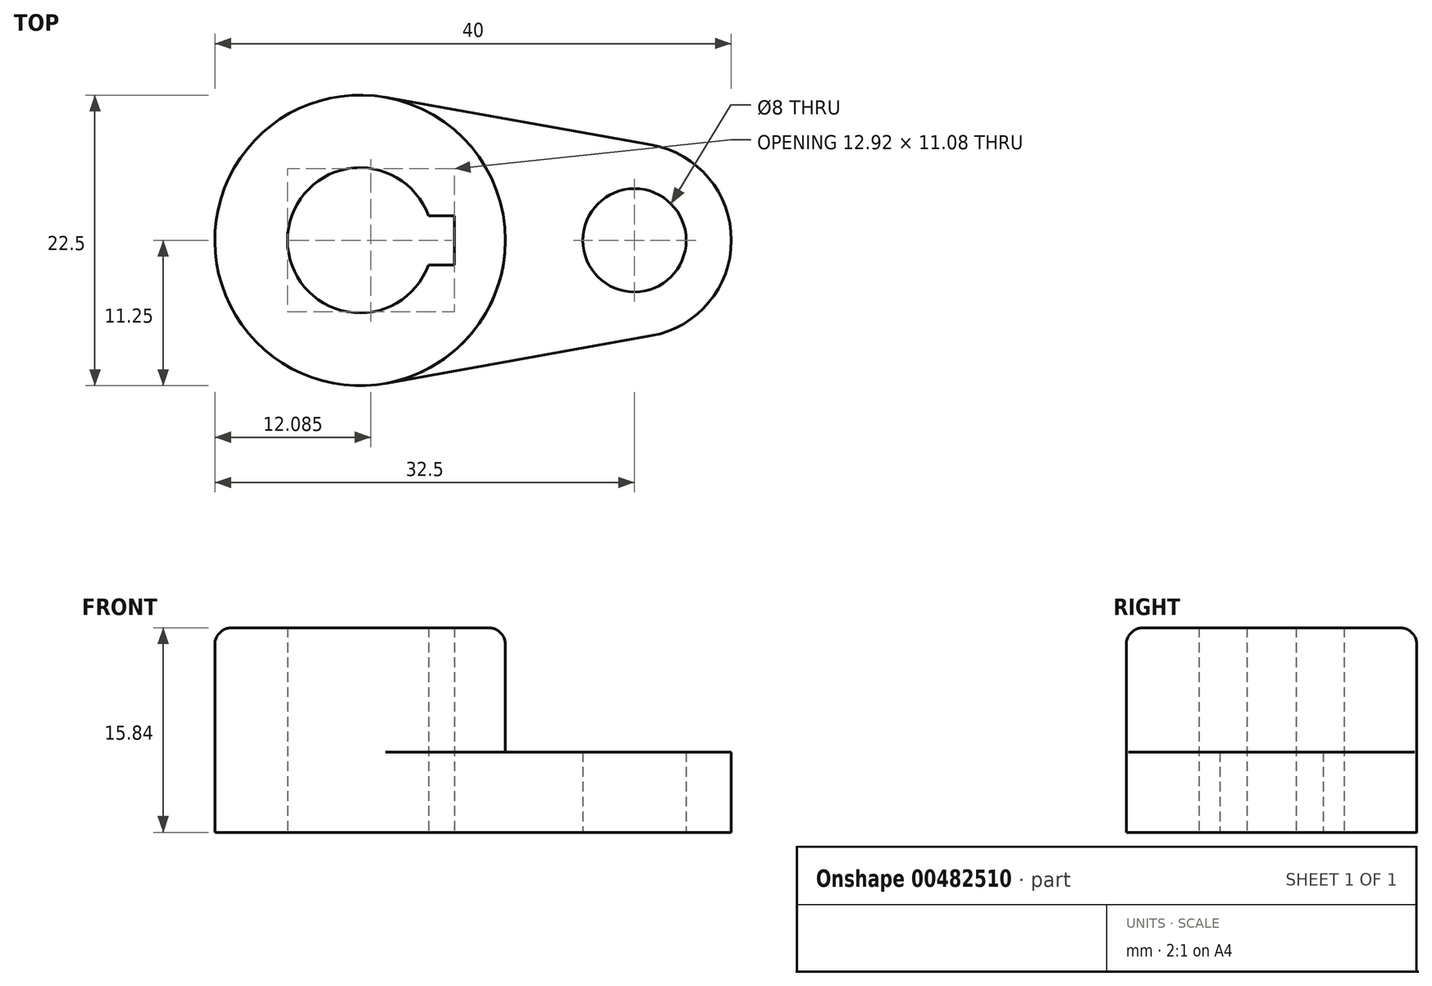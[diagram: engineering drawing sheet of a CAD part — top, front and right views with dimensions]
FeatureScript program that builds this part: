
annotation { "Feature Type Name" : "Feature", "Feature Type Description" : "" }
export const myFeature = defineFeature(function(context is Context, id is Id, definition is map)
    precondition{}
    {
        {
            var Q0;
            Q0=qCreatedBy(makeId("Top.planeOp"),FACE);
            var sketch = newSketch(context, id + "F0", { "sketchPlane" : qUnion([Q0])});
            skCircle(sketch, "E0", {"center": v(0, 0) * mm, "radius": 11.25 * mm});
            skCircle(sketch, "E1", {"center": v(0, 0) * mm, "radius": 5.62 * mm});
            skLineSegment(sketch, "E2.top", {"start": v(-5.3, -1.9) * mm, "end": v(7.3, -1.9) * mm});
            skLineSegment(sketch, "E2.right", {"start": v(7.3, 0) * mm, "end": v(7.3, -1.9) * mm});
            skLineSegment(sketch, "E3.MirrorCS", {"start": v(-5.3, 1.9) * mm, "end": v(7.3, 1.9) * mm});
            skLineSegment(sketch, "E4.MirrorCS", {"start": v(7.3, 0) * mm, "end": v(7.3, 1.9) * mm});
            skCircle(sketch, "E5", {"center": v(21.25, 0) * mm, "radius": 4 * mm});
            skLineSegment(sketch, "E6", {"start": v(21.25, 0) * mm, "end": v(27.42, 4.27) * mm});
            skArc(sketch, "E7", {"start": v(22.57, -7.38) * mm, "mid": v(28.75, 0) * mm, "end": v(22.57, 7.38) * mm});
            skLineSegment(sketch, "E8", {"start": v(1.99, 11.07) * mm, "end": v(22.57, 7.38) * mm});
            skLineSegment(sketch, "E9", {"start": v(1.99, -11.07) * mm, "end": v(22.57, -7.38) * mm});
            skPoint(sketch, "E2.left.start.orphan", {"position": v(-5.62, 0) * mm});
            skSolve(sketch);
        }
        {
            var Q0;
            {var subQ11=sQuery(id+"F0.wireOp",EDGE,"E2.right");Q0=makeQuery(id+"F0.imprint","IMPRINT",FACE,{"disambiguationData":[TD([[makeQuery(id+"F0.imprint","IMPRINT",EDGE,{"derivedFrom":subQ11}),1.0]])]});}
            extrude(context, id + "F1", {"entities" : qUnion([Q0]), "depth" : 15.84 * mm});
        }
        {
            var Q0;
            Q0=makeQuery(id+"F0.imprint","IMPRINT",FACE,{"disambiguationData":[TD([[makeQuery(id+"F0.imprint","IMPRINT",EDGE,{"derivedFrom":sQuery(id+"F0.wireOp",EDGE,"E5")}),-1.0]])]});
            extrude(context, id + "F2", {"entities" : qUnion([Q0]), "operationType" : NewBodyOperationType.ADD, "depth" : 6.2 * mm});
        }
        {
            var Q0;
            Q0=makeQuery(id+"F1.opExtrude","CAP_EDGE",EDGE,{"disambiguationData":[OSD([sQuery(id+"F0.wireOp",EDGE,"E0")])],"isStart":false});
            fillet(context, id + "F3", {"entities" : qUnion([Q0]), "radius" : 1.3 * mm, "tangentPropagation" : true, "allowEdgeOverflow" : false});
        }
    });
